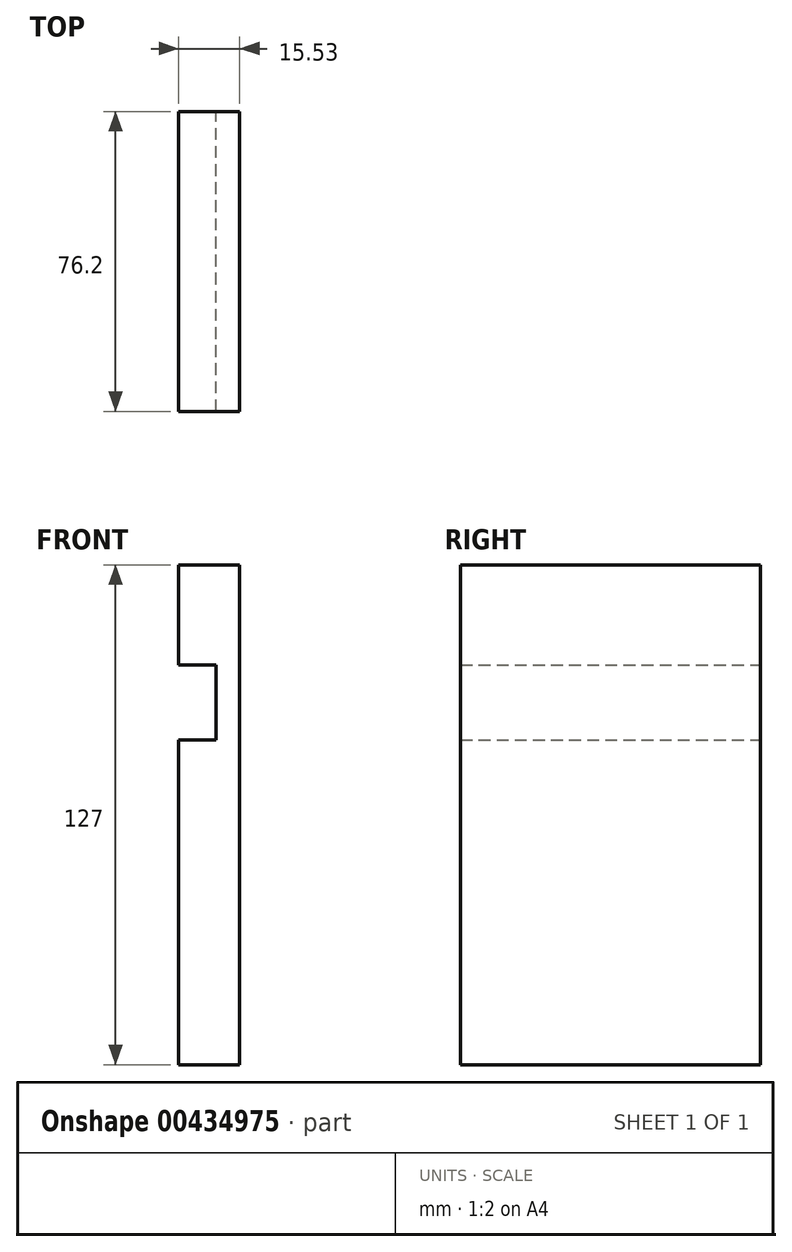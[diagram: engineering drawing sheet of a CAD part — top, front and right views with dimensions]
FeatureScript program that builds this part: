
annotation { "Feature Type Name" : "Feature", "Feature Type Description" : "" }
export const myFeature = defineFeature(function(context is Context, id is Id, definition is map)
    precondition{}
    {
        {
            var Q0;
            Q0=qCreatedBy(makeId("Front.planeOp"),FACE);
            var sketch = newSketch(context, id + "F0", { "sketchPlane" : qUnion([Q0])});
            skLineSegment(sketch, "E0", {"start": v(0, 0) * mm, "end": v(0, 127) * mm});
            skLineSegment(sketch, "E1", {"start": v(0, 127) * mm, "end": v(-15.53, 127) * mm});
            skLineSegment(sketch, "E2", {"start": v(-15.53, 127) * mm, "end": v(-15.53, 101.6) * mm});
            skLineSegment(sketch, "E3", {"start": v(-15.53, 101.6) * mm, "end": v(-6, 101.6) * mm});
            skLineSegment(sketch, "E4", {"start": v(-6, 101.6) * mm, "end": v(-6, 82.55) * mm});
            skLineSegment(sketch, "E5", {"start": v(-6, 82.55) * mm, "end": v(-15.53, 82.55) * mm});
            skLineSegment(sketch, "E6", {"start": v(-15.53, 82.55) * mm, "end": v(-15.53, 0) * mm});
            skLineSegment(sketch, "E7", {"start": v(-15.53, 0) * mm, "end": v(0, 0) * mm});
            skSolve(sketch);
        }
        {
            var Q0;
            Q0=makeQuery(id+"F0.imprint","IMPRINT",FACE,{"disambiguationData":[TD([[makeQuery(id+"F0.imprint","IMPRINT",EDGE,{"derivedFrom":sQuery(id+"F0.wireOp",EDGE,"E0")}),1.0]])]});
            extrude(context, id + "F1", {"entities" : qUnion([Q0]), "depth" : 76.2 * mm});
        }
    });
